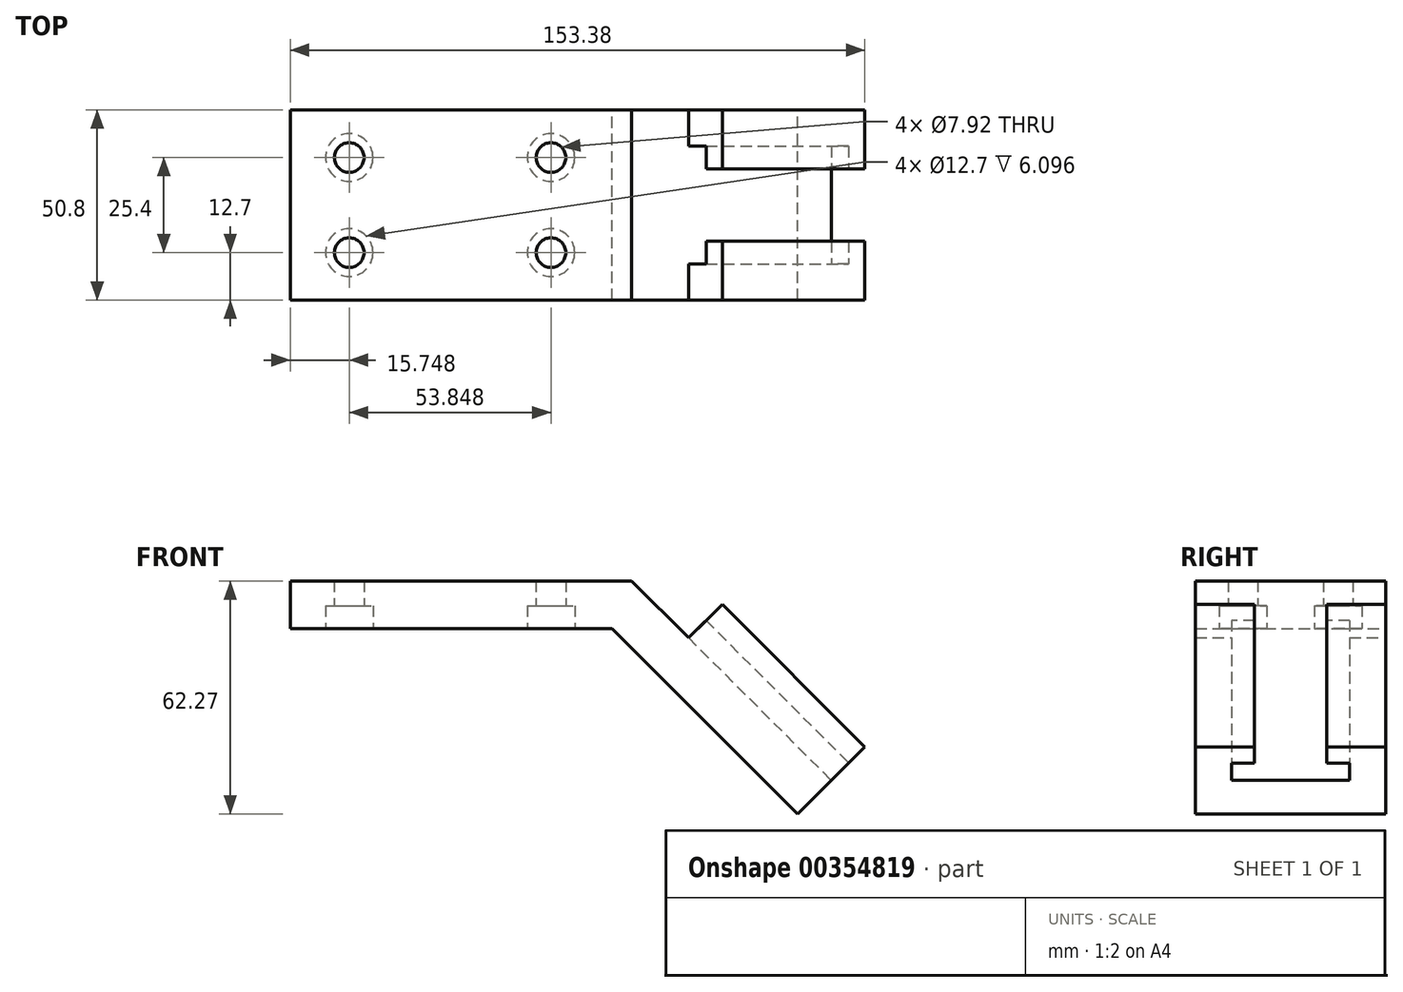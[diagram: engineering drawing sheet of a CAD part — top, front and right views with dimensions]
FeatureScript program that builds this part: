
annotation { "Feature Type Name" : "Feature", "Feature Type Description" : "" }
export const myFeature = defineFeature(function(context is Context, id is Id, definition is map)
    precondition{}
    {
        {
            var Q0;
            Q0=qCreatedBy(makeId("Front.planeOp"),FACE);
            var sketch = newSketch(context, id + "F0", { "sketchPlane" : qUnion([Q0])});
            skLineSegment(sketch, "E0", {"start": v(0, 0) * mm, "end": v(85.85, 0) * mm});
            skLineSegment(sketch, "E1", {"start": v(0, 0) * mm, "end": v(0, 12.7) * mm});
            skLineSegment(sketch, "E2", {"start": v(0, 12.7) * mm, "end": v(91.11, 12.7) * mm});
            skLineSegment(sketch, "E3", {"start": v(85.85, 0) * mm, "end": v(135.42, -49.57) * mm});
            skLineSegment(sketch, "E4", {"start": v(135.42, -49.57) * mm, "end": v(153.38, -31.61) * mm});
            skLineSegment(sketch, "E5", {"start": v(153.38, -31.61) * mm, "end": v(115.3, 6.47) * mm});
            skLineSegment(sketch, "E6", {"start": v(115.3, 6.47) * mm, "end": v(106.33, -2.51) * mm});
            skLineSegment(sketch, "E7", {"start": v(106.33, -2.51) * mm, "end": v(91.11, 12.7) * mm});
            skLineSegment(sketch, "E8", {"start": v(106.33, -2.51) * mm, "end": v(76.42, 27.4) * mm, "construction": true});
            skSolve(sketch);
        }
        {
            var Q0;
            Q0 = qSketchRegion(id + "F0", true);
            extrude(context, id + "F1", {"entities" : qUnion([Q0]), "endBound" : BoundingType.SYMMETRIC, "depth" : 50.8 * mm});
        }
        {
            var Q0;
            Q0=makeQuery(id+"F1.opExtrude","SWEPT_FACE",FACE,{"disambiguationData":[OSD([sQuery(id+"F0.wireOp",EDGE,"E0")])]});
            var sketch = newSketch(context, id + "F2", { "sketchPlane" : qUnion([Q0])});
            skPoint(sketch, "E9", {"position": v(15.75, 12.7) * mm});
            skPoint(sketch, "E10", {"position": v(69.6, 12.7) * mm});
            skPoint(sketch, "E11", {"position": v(15.75, -12.7) * mm});
            skPoint(sketch, "E12", {"position": v(69.6, -12.7) * mm});
            skSolve(sketch);
        }
        {
            var Q0;
            Q0=sQuery(id+"F2.wireOp",VERTEX,"E9");
            var Q1;
            Q1=sQuery(id+"F2.wireOp",VERTEX,"E11");
            var Q2;
            Q2=sQuery(id+"F2.wireOp",VERTEX,"E10");
            var Q3;
            Q3=sQuery(id+"F2.wireOp",VERTEX,"E12");
            var Q4;
            Q4=makeQuery(id+"F1.opExtrude","SWEPT_BODY",BODY,{"disambiguationData":[OSD([sQuery(id+"F0.wireOp",EDGE,"E0"),sQuery(id+"F0.wireOp",EDGE,"E1"),sQuery(id+"F0.wireOp",EDGE,"E2"),sQuery(id+"F0.wireOp",EDGE,"E3"),sQuery(id+"F0.wireOp",EDGE,"E4"),sQuery(id+"F0.wireOp",EDGE,"E5"),sQuery(id+"F0.wireOp",EDGE,"E6"),sQuery(id+"F0.wireOp",EDGE,"E7")])]});
            hole(context, id + "F3", {"style" : HoleStyle.C_BORE, "endStyle" : HoleEndStyle.THROUGH, "holeDiameter" : 7.92 * mm, "cBoreDiameter" : 12.7 * mm, "cBoreDepth" : 6.1 * mm, "isTappedThrough" : true, "tappedDepth" : 12.7 * mm, "tapClearance" : 3, "locations" : qUnion([Q0, Q1, Q2, Q3]), "scope" : qUnion([Q4])});
        }
        {
            var Q0;
            Q0=makeQuery(id+"F1.opExtrude","SWEPT_FACE",FACE,{"disambiguationData":[OSD([sQuery(id+"F0.wireOp",EDGE,"E5")])]});
            var sketch = newSketch(context, id + "F4", { "sketchPlane" : qUnion([Q0])});
            skLineSegment(sketch, "E13", {"start": v(76.96, 0) * mm, "end": v(130.81, 0) * mm, "construction": true});
            skArc(sketch, "E14", {"start": v(124.44, -25.4) * mm, "mid": v(130.81, 0) * mm, "end": v(124.44, 25.4) * mm});
            skLineSegment(sketch, "E15", {"start": v(124.44, 25.4) * mm, "end": v(130.81, 25.4) * mm});
            skLineSegment(sketch, "E16", {"start": v(130.81, 25.4) * mm, "end": v(130.81, -25.4) * mm});
            skLineSegment(sketch, "E17", {"start": v(130.81, -25.4) * mm, "end": v(124.44, -25.4) * mm});
            skLineSegment(sketch, "E18", {"start": v(124.44, -25.4) * mm, "end": v(76.96, -25.4) * mm});
            skLineSegment(sketch, "E19", {"start": v(76.96, -25.4) * mm, "end": v(76.96, -9.65) * mm});
            skLineSegment(sketch, "E20", {"start": v(76.96, -9.65) * mm, "end": v(129.94, -9.65) * mm});
            skLineSegment(sketch, "E21", {"start": v(76.96, 25.4) * mm, "end": v(76.96, 9.65) * mm});
            skLineSegment(sketch, "E22", {"start": v(76.96, 9.65) * mm, "end": v(129.94, 9.65) * mm});
            skSolve(sketch);
        }
        {
            var Q0;
            {var subQ0=sQuery(id+"F4.wireOp",EDGE,"E17");Q0=makeQuery(id+"F4.imprint","IMPRINT",FACE,{"disambiguationData":[TD([[makeQuery(id+"F4.imprint","IMPRINT",EDGE,{"derivedFrom":subQ0}),-1.0]])]});}
            var Q1;
            {var subQ4=sQuery(id+"F4.wireOp",EDGE,"E15");Q1=makeQuery(id+"F4.imprint","IMPRINT",FACE,{"disambiguationData":[TD([[makeQuery(id+"F4.imprint","IMPRINT",EDGE,{"derivedFrom":subQ4}),1.0]])]});}
            extrude(context, id + "F5", {"entities" : qUnion([Q0, Q1]), "operationType" : NewBodyOperationType.REMOVE, "oppositeDirection" : true, "depth" : 25.4 * mm});
        }
        {
            var Q0;
            Q0=qCreatedBy(makeId("Front.planeOp"),FACE);
            var sketch = newSketch(context, id + "F6", { "sketchPlane" : qUnion([Q0])});
            skLineSegment(sketch, "E23", {"start": v(115.3, 6.47) * mm, "end": v(153.38, -31.61) * mm});
            skLineSegment(sketch, "E24", {"start": v(115.3, 6.47) * mm, "end": v(111, 2.16) * mm});
            skLineSegment(sketch, "E25", {"start": v(111, 2.16) * mm, "end": v(149.07, -35.92) * mm});
            skLineSegment(sketch, "E26", {"start": v(153.38, -31.61) * mm, "end": v(149.07, -35.92) * mm});
            skLineSegment(sketch, "E27", {"start": v(111, 2.16) * mm, "end": v(106.33, -2.51) * mm});
            skLineSegment(sketch, "E28", {"start": v(106.33, -2.51) * mm, "end": v(144.4, -40.6) * mm});
            skLineSegment(sketch, "E29", {"start": v(149.07, -35.92) * mm, "end": v(144.4, -40.6) * mm});
            skSolve(sketch);
        }
        {
            var Q0;
            Q0 = qSketchRegion(id + "F6", true);
            var Q1;
            Q1=sQuery(id+"F6.wireOp",EDGE,"E25");
            var Q2;
            Q2=sQuery(id+"F6.wireOp",EDGE,"E23");
            var Q3;
            Q3=sQuery(id+"F6.wireOp",EDGE,"E26");
            var Q4;
            Q4=sQuery(id+"F6.wireOp",EDGE,"E24");
            extrude(context, id + "F7", {"entities" : qUnion([Q0]), "operationType" : NewBodyOperationType.REMOVE, "surfaceEntities" : qUnion([Q1, Q2, Q3, Q4]), "endBound" : BoundingType.SYMMETRIC, "oppositeDirection" : true, "depth" : 19.3 * mm});
        }
        {
            var Q0;
            Q0=makeQuery(id+"F6.imprint","IMPRINT",FACE,{"disambiguationData":[TD([[makeQuery(id+"F6.imprint","IMPRINT",EDGE,{"derivedFrom":sQuery(id+"F6.wireOp",EDGE,"E25")}),-1.0]])]});
            extrude(context, id + "F8", {"entities" : qUnion([Q0]), "operationType" : NewBodyOperationType.REMOVE, "endBound" : BoundingType.SYMMETRIC, "oppositeDirection" : true, "depth" : 31.5 * mm});
        }
    });
